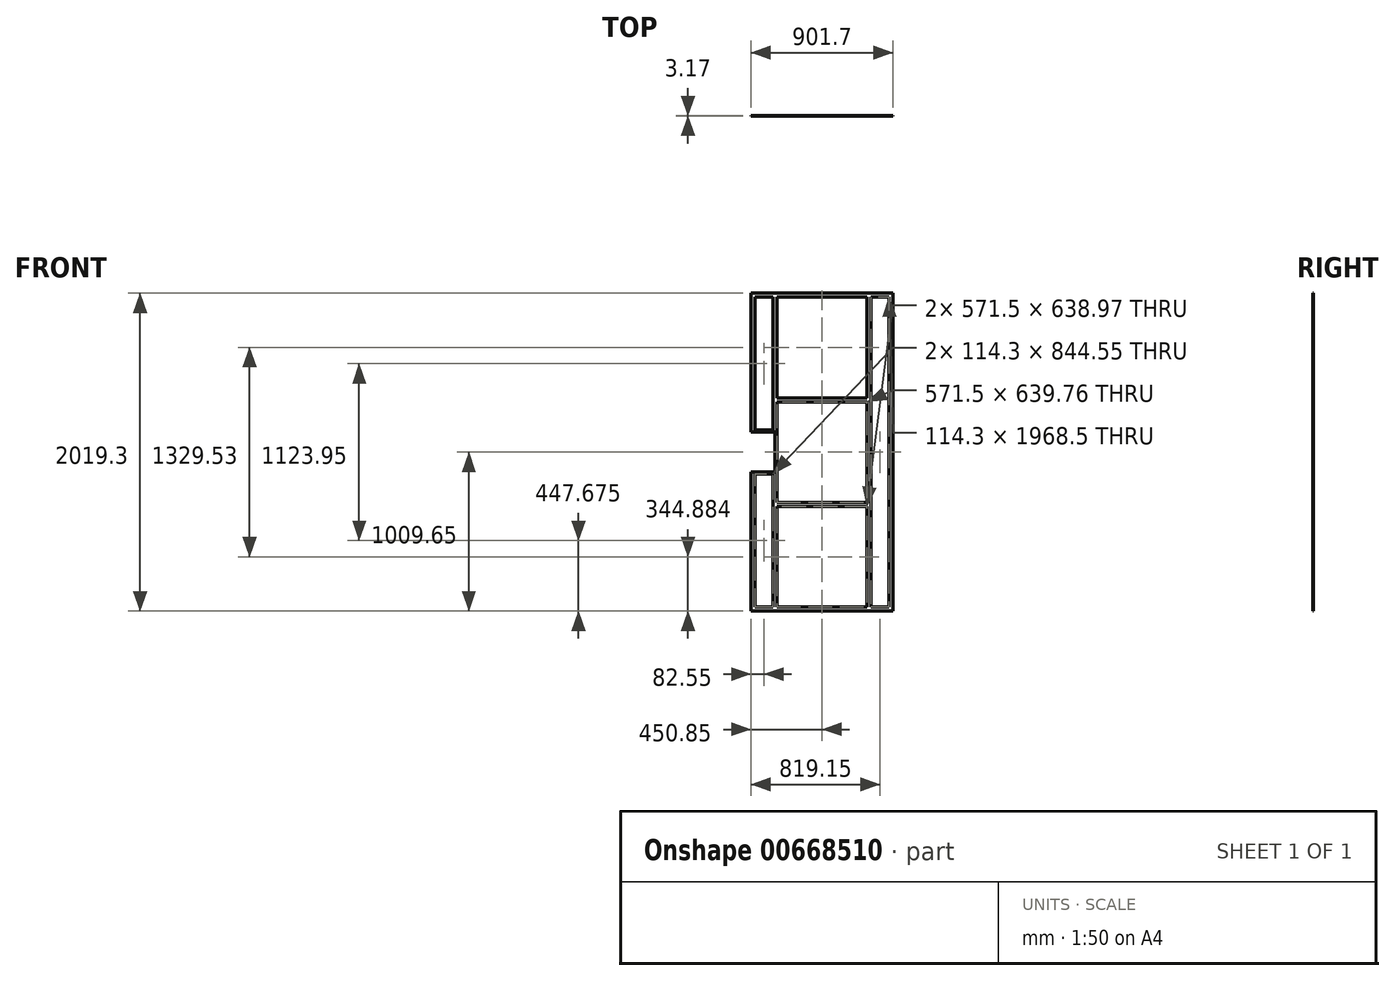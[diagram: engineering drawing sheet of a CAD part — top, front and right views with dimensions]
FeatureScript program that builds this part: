
annotation { "Feature Type Name" : "Feature", "Feature Type Description" : "" }
export const myFeature = defineFeature(function(context is Context, id is Id, definition is map)
    precondition{}
    {
        {
            var Q0;
            Q0=qCreatedBy(makeId("Front.planeOp"),FACE);
            var sketch = newSketch(context, id + "F0", { "sketchPlane" : qUnion([Q0])});
            skLineSegment(sketch, "E0.top", {"start": v(-736.6, 1993.9) * mm, "end": v(-165.1, 1993.9) * mm});
            skPoint(sketch, "E0.middle", {"position": v(-584.82, 2240.76) * mm});
            skLineSegment(sketch, "E1.0", {"start": v(-736.6, 25.4) * mm, "end": v(-165.1, 25.4) * mm});
            skLineSegment(sketch, "E2", {"start": v(-139.7, 1993.9) * mm, "end": v(-139.7, 25.4) * mm});
            skLineSegment(sketch, "E3", {"start": v(-139.7, 25.4) * mm, "end": v(-25.4, 25.4) * mm});
            skLineSegment(sketch, "E4", {"start": v(-25.4, 25.4) * mm, "end": v(-25.4, 1993.9) * mm});
            skLineSegment(sketch, "E5", {"start": v(-25.4, 1993.9) * mm, "end": v(-139.7, 1993.9) * mm});
            skLineSegment(sketch, "E6", {"start": v(-762, 25.4) * mm, "end": v(-762, 869.95) * mm});
            skLineSegment(sketch, "E7", {"start": v(-762, 869.95) * mm, "end": v(-876.3, 869.95) * mm});
            skLineSegment(sketch, "E8", {"start": v(-876.3, 869.95) * mm, "end": v(-876.3, 25.4) * mm});
            skLineSegment(sketch, "E9", {"start": v(-876.3, 25.4) * mm, "end": v(-762, 25.4) * mm});
            skLineSegment(sketch, "E10", {"start": v(-762, 1993.9) * mm, "end": v(-876.3, 1993.9) * mm});
            skLineSegment(sketch, "E11", {"start": v(-876.3, 1993.9) * mm, "end": v(-876.3, 1149.35) * mm});
            skLineSegment(sketch, "E12", {"start": v(-762, 1993.9) * mm, "end": v(-762, 1149.35) * mm});
            skLineSegment(sketch, "E13", {"start": v(-762, 1149.35) * mm, "end": v(-876.3, 1149.35) * mm});
            skLineSegment(sketch, "E14.0", {"start": v(0, 0) * mm, "end": v(0, 2019.3) * mm});
            skLineSegment(sketch, "E15", {"start": v(0, 2019.3) * mm, "end": v(-901.7, 2019.3) * mm});
            skLineSegment(sketch, "E16", {"start": v(-901.7, 2019.3) * mm, "end": v(-901.7, 1136.65) * mm});
            skLineSegment(sketch, "E17", {"start": v(-901.7, 1136.65) * mm, "end": v(-749.3, 1136.65) * mm});
            skLineSegment(sketch, "E18", {"start": v(-749.3, 1136.65) * mm, "end": v(-749.3, 882.65) * mm});
            skLineSegment(sketch, "E19", {"start": v(-749.3, 882.65) * mm, "end": v(-901.7, 882.65) * mm});
            skLineSegment(sketch, "E20", {"start": v(-901.7, 882.65) * mm, "end": v(-901.7, 0) * mm});
            skLineSegment(sketch, "E21", {"start": v(-901.7, 0) * mm, "end": v(0, 0) * mm});
            skLineSegment(sketch, "E22", {"start": v(-736.6, 1993.9) * mm, "end": v(-736.6, 25.4) * mm});
            skLineSegment(sketch, "E23", {"start": v(-165.1, 25.4) * mm, "end": v(-165.1, 1993.9) * mm});
            skLineSegment(sketch, "E24", {"start": v(-736.6, 689.77) * mm, "end": v(-165.1, 689.77) * mm});
            skLineSegment(sketch, "E25", {"start": v(-736.6, 1354.93) * mm, "end": v(-165.1, 1354.93) * mm});
            skLineSegment(sketch, "E26", {"start": v(-736.6, 1329.53) * mm, "end": v(-165.1, 1329.53) * mm});
            skLineSegment(sketch, "E27", {"start": v(-736.6, 664.37) * mm, "end": v(-165.1, 664.37) * mm});
            skSolve(sketch);
        }
        {
            var Q0;
            Q0 = qSketchRegion(id + "F0", true);
            var Q1;
            {var subQ0=sQuery(id+"F0.wireOp",EDGE,"E25");Q1=makeQuery(id+"F0.imprint","IMPRINT",FACE,{"disambiguationData":[TD([[makeQuery(id+"F0.imprint","IMPRINT",EDGE,{"derivedFrom":subQ0}),-1.0]])]});}
            var Q2;
            {var subQ0=sQuery(id+"F0.wireOp",EDGE,"E24");Q2=makeQuery(id+"F0.imprint","IMPRINT",FACE,{"disambiguationData":[TD([[makeQuery(id+"F0.imprint","IMPRINT",EDGE,{"derivedFrom":subQ0}),-1.0]])]});}
            extrude(context, id + "F1", {"entities" : qUnion([Q0, Q1, Q2]), "depth" : 3.17 * mm, "offsetDistance" : 25.4 * mm});
        }
    });
